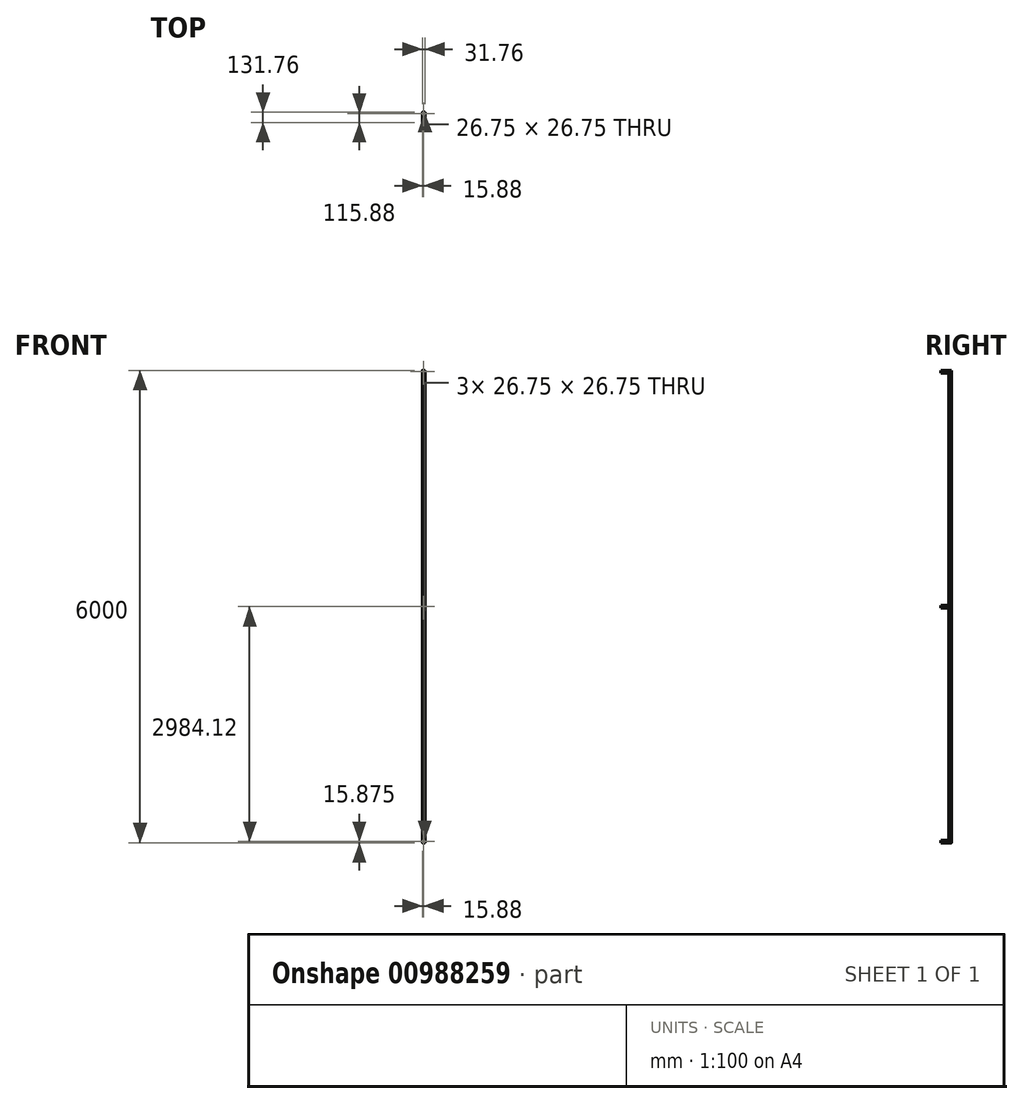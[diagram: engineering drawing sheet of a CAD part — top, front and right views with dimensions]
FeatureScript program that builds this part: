
annotation { "Feature Type Name" : "Feature", "Feature Type Description" : "" }
export const myFeature = defineFeature(function(context is Context, id is Id, definition is map)
    precondition{}
    {
        {
            var Q0;
            Q0=qCreatedBy(makeId("Top.planeOp"),FACE);
            var sketch = newSketch(context, id + "F0", { "sketchPlane" : qUnion([Q0])});
            skLineSegment(sketch, "E0.bottom", {"start": v(13.38, 15.88) * mm, "end": v(-13.38, 15.88) * mm});
            skLineSegment(sketch, "E0.top", {"start": v(13.37, -15.88) * mm, "end": v(-13.37, -15.88) * mm});
            skLineSegment(sketch, "E0.left", {"start": v(15.88, 13.38) * mm, "end": v(15.88, -13.37) * mm});
            skLineSegment(sketch, "E0.right", {"start": v(-15.88, 13.38) * mm, "end": v(-15.88, -13.37) * mm});
            skPoint(sketch, "E0.middle", {"position": v(0, 0) * mm});
            skPoint(sketch, "E1.visualSharp", {"position": v(-15.88, 15.88) * mm});
            skArc(sketch, "E1.filletArc", {"start": v(-13.38, 15.88) * mm, "mid": v(-15.14, 15.14) * mm, "end": v(-15.88, 13.38) * mm});
            skPoint(sketch, "E2.visualSharp", {"position": v(15.88, 15.88) * mm});
            skArc(sketch, "E2.filletArc", {"start": v(15.88, 13.38) * mm, "mid": v(15.14, 15.14) * mm, "end": v(13.38, 15.88) * mm});
            skPoint(sketch, "E3.visualSharp", {"position": v(15.88, -15.88) * mm});
            skArc(sketch, "E3.filletArc", {"start": v(13.37, -15.88) * mm, "mid": v(15.14, -15.14) * mm, "end": v(15.88, -13.37) * mm});
            skPoint(sketch, "E4.visualSharp", {"position": v(-15.88, -15.88) * mm});
            skArc(sketch, "E4.filletArc", {"start": v(-15.88, -13.37) * mm, "mid": v(-15.14, -15.14) * mm, "end": v(-13.37, -15.88) * mm});
            skLineSegment(sketch, "E5.0", {"start": v(13.38, 13.38) * mm, "end": v(13.38, 13.38) * mm});
            skLineSegment(sketch, "E5.1", {"start": v(13.38, 13.38) * mm, "end": v(13.38, -13.38) * mm});
            skLineSegment(sketch, "E5.2", {"start": v(13.38, 13.38) * mm, "end": v(-13.37, 13.38) * mm});
            skLineSegment(sketch, "E5.3", {"start": v(13.37, -13.37) * mm, "end": v(13.37, -13.37) * mm});
            skLineSegment(sketch, "E5.4", {"start": v(-13.37, 13.37) * mm, "end": v(-13.37, 13.37) * mm});
            skLineSegment(sketch, "E5.5", {"start": v(-13.37, 13.38) * mm, "end": v(-13.37, -13.38) * mm});
            skLineSegment(sketch, "E5.6", {"start": v(-13.37, -13.37) * mm, "end": v(-13.37, -13.37) * mm});
            skLineSegment(sketch, "E5.7", {"start": v(13.38, -13.38) * mm, "end": v(-13.37, -13.38) * mm});
            skSolve(sketch);
        }
        {
            var Q0;
            Q0=makeQuery(id+"F0.imprint","IMPRINT",FACE,{"disambiguationData":[TD([[makeQuery(id+"F0.imprint","IMPRINT",EDGE,{"derivedFrom":sQuery(id+"F0.wireOp",EDGE,"E0.bottom")}),1.0]])]});
            extrude(context, id + "F1", {"entities" : qUnion([Q0]), "depth" : 6000 * mm, "offsetDistance" : 25 * mm});
        }
        {
            var Q0;
            Q0=makeQuery(id+"F1.opExtrude","SWEPT_FACE",FACE,{"disambiguationData":[OSD([sQuery(id+"F0.wireOp",EDGE,"E0.top")])]});
            var sketch = newSketch(context, id + "F2", { "sketchPlane" : qUnion([Q0])});
            skLineSegment(sketch, "E6.bottom", {"start": v(13.38, 2984.12) * mm, "end": v(-13.38, 2984.12) * mm});
            skLineSegment(sketch, "E6.top", {"start": v(13.38, 3015.88) * mm, "end": v(-13.38, 3015.88) * mm});
            skLineSegment(sketch, "E6.left", {"start": v(15.88, 2986.62) * mm, "end": v(15.88, 3013.38) * mm});
            skLineSegment(sketch, "E6.right", {"start": v(-15.87, 2986.62) * mm, "end": v(-15.87, 3013.38) * mm});
            skPoint(sketch, "E6.middle", {"position": v(0, 3000) * mm});
            skPoint(sketch, "E7.visualSharp", {"position": v(15.88, 3015.88) * mm});
            skArc(sketch, "E7.filletArc", {"start": v(15.88, 3013.38) * mm, "mid": v(15.14, 3015.14) * mm, "end": v(13.38, 3015.88) * mm});
            skPoint(sketch, "E8.visualSharp", {"position": v(15.88, 2984.12) * mm});
            skArc(sketch, "E8.filletArc", {"start": v(13.38, 2984.12) * mm, "mid": v(15.14, 2984.86) * mm, "end": v(15.87, 2986.62) * mm});
            skPoint(sketch, "E9.visualSharp", {"position": v(-15.87, 2984.12) * mm});
            skArc(sketch, "E9.filletArc", {"start": v(-15.87, 2986.62) * mm, "mid": v(-15.14, 2984.86) * mm, "end": v(-13.38, 2984.12) * mm});
            skPoint(sketch, "E10.visualSharp", {"position": v(-15.87, 3015.88) * mm});
            skArc(sketch, "E10.filletArc", {"start": v(-13.38, 3015.88) * mm, "mid": v(-15.14, 3015.14) * mm, "end": v(-15.88, 3013.38) * mm});
            skLineSegment(sketch, "E11.0", {"start": v(13.38, 3013.38) * mm, "end": v(-13.37, 3013.38) * mm});
            skLineSegment(sketch, "E11.1", {"start": v(13.38, 2986.62) * mm, "end": v(13.38, 3013.38) * mm});
            skLineSegment(sketch, "E11.2", {"start": v(13.38, 2986.62) * mm, "end": v(-13.37, 2986.62) * mm});
            skLineSegment(sketch, "E11.3", {"start": v(-13.37, 2986.62) * mm, "end": v(-13.37, 3013.38) * mm});
            skLineSegment(sketch, "E12.bottom", {"start": v(13.38, 5968.25) * mm, "end": v(-13.37, 5968.25) * mm});
            skLineSegment(sketch, "E12.top", {"start": v(13.38, 6000) * mm, "end": v(-13.37, 6000) * mm});
            skLineSegment(sketch, "E12.left", {"start": v(15.88, 5970.75) * mm, "end": v(15.88, 5997.5) * mm});
            skLineSegment(sketch, "E12.right", {"start": v(-15.87, 5970.75) * mm, "end": v(-15.87, 5997.5) * mm});
            skPoint(sketch, "E12.middle", {"position": v(0, 5984.13) * mm});
            skPoint(sketch, "E13.visualSharp", {"position": v(15.88, 6000) * mm});
            skArc(sketch, "E13.filletArc", {"start": v(15.88, 5997.5) * mm, "mid": v(15.14, 5999.27) * mm, "end": v(13.38, 6000) * mm});
            skPoint(sketch, "E14.visualSharp", {"position": v(15.88, 5968.25) * mm});
            skArc(sketch, "E14.filletArc", {"start": v(13.38, 5968.25) * mm, "mid": v(15.14, 5968.98) * mm, "end": v(15.88, 5970.75) * mm});
            skPoint(sketch, "E15.visualSharp", {"position": v(-15.87, 5968.25) * mm});
            skArc(sketch, "E15.filletArc", {"start": v(-15.87, 5970.75) * mm, "mid": v(-15.14, 5968.98) * mm, "end": v(-13.37, 5968.25) * mm});
            skPoint(sketch, "E16.visualSharp", {"position": v(-15.87, 6000) * mm});
            skArc(sketch, "E16.filletArc", {"start": v(-13.37, 6000) * mm, "mid": v(-15.14, 5999.27) * mm, "end": v(-15.87, 5997.5) * mm});
            skLineSegment(sketch, "E17.0", {"start": v(13.37, 5997.5) * mm, "end": v(-13.37, 5997.5) * mm});
            skLineSegment(sketch, "E17.1", {"start": v(13.38, 5970.75) * mm, "end": v(13.37, 5997.5) * mm});
            skLineSegment(sketch, "E17.2", {"start": v(13.38, 5970.75) * mm, "end": v(-13.37, 5970.75) * mm});
            skLineSegment(sketch, "E17.3", {"start": v(-13.37, 5970.75) * mm, "end": v(-13.37, 5997.5) * mm});
            skLineSegment(sketch, "E18.bottom", {"start": v(13.37, 0) * mm, "end": v(-13.38, 0) * mm});
            skLineSegment(sketch, "E18.top", {"start": v(13.37, 31.75) * mm, "end": v(-13.37, 31.75) * mm});
            skLineSegment(sketch, "E18.left", {"start": v(15.87, 2.5) * mm, "end": v(15.87, 29.25) * mm});
            skLineSegment(sketch, "E18.right", {"start": v(-15.88, 2.5) * mm, "end": v(-15.88, 29.25) * mm});
            skPoint(sketch, "E18.middle", {"position": v(0, 15.88) * mm});
            skPoint(sketch, "E19.visualSharp", {"position": v(15.87, 31.75) * mm});
            skArc(sketch, "E19.filletArc", {"start": v(15.87, 29.25) * mm, "mid": v(15.14, 31.02) * mm, "end": v(13.37, 31.75) * mm});
            skPoint(sketch, "E20.visualSharp", {"position": v(15.87, 0) * mm});
            skArc(sketch, "E20.filletArc", {"start": v(13.37, 0) * mm, "mid": v(15.14, 0.73) * mm, "end": v(15.87, 2.5) * mm});
            skPoint(sketch, "E21.visualSharp", {"position": v(-15.88, 0) * mm});
            skArc(sketch, "E21.filletArc", {"start": v(-15.88, 2.5) * mm, "mid": v(-15.14, 0.73) * mm, "end": v(-13.38, 0) * mm});
            skPoint(sketch, "E22.visualSharp", {"position": v(-15.88, 31.75) * mm});
            skArc(sketch, "E22.filletArc", {"start": v(-13.37, 31.75) * mm, "mid": v(-15.14, 31.02) * mm, "end": v(-15.88, 29.25) * mm});
            skLineSegment(sketch, "E23.0", {"start": v(13.37, 29.25) * mm, "end": v(-13.38, 29.25) * mm});
            skLineSegment(sketch, "E23.1", {"start": v(13.37, 2.5) * mm, "end": v(13.37, 29.25) * mm});
            skLineSegment(sketch, "E23.2", {"start": v(13.37, 2.5) * mm, "end": v(-13.38, 2.5) * mm});
            skLineSegment(sketch, "E23.3", {"start": v(-13.38, 2.5) * mm, "end": v(-13.38, 29.25) * mm});
            skSolve(sketch);
        }
        {
            var Q0;
            Q0 = qSketchRegion(id + "F2", true);
            extrude(context, id + "F3", {"entities" : qUnion([Q0]), "surfaceOperationType" : NewSurfaceOperationType.ADD, "depth" : 100 * mm, "offsetDistance" : 25 * mm});
        }
    });
